AUTODESK INVENTOR PART (.ipt)
format: ipt  version: 2015 (Build 190159000, 159)  size: 84,480 bytes
history: native  units: mm
features: sketch x1
ambient origin geometry x8: Origin, YZ Plane, XZ Plane, XY Plane, X Axis, Y Axis, Z Axis, Center Point
feature tree (1):
  sketch  "Sketch1"  dims[d0=210.0mm d1=35.0mm d2=5.0mm d3=285.0mm d4=22.0mm d5=10.0mm d7=5.0mm d8=2.0mm d9=1.0mm d10=1.0mm d14=3.0mm d15=3.0mm d16=3.0mm d17=3.0mm]
